# Revit family: OLYMPIA 24 X 96
name_source: partatom
category: Generic Models
units: mm (PartAtom-declared; Revit-internal decimal feet)

## family parameters
Can host rebar = No
Cut with Voids When Loaded = No
Host = Face
Maintain Annotation Orientation = No
Part Type = Normal
Room Calculation Point = No
Round Connector Dimension = Use Diameter
Shared = No

## types (11) — shared parameters
1/2 STICK = 4' - 0"
Default Elevation = 4' - 0"
PANEL LENGTH = 8' - 0"
PANEL MATERIAL = WF - PLYWOOD
PANEL WIDTH = 2' - 0"
STICKS PER WIDTH = 8

## per-type parameters (varying)
| type | CLADDING MATERIAL |
| OLYMPIA 24 X 96 - BONE | WF - CASCADES / OLYMPIA - BONE |
| OLYMPIA 24 X 96 - CITRINE | WF - CASCADES / OLYMPIA - CITRINE |
| OLYMPIA 24 X 96 - AUBURN | WF - CASCADES / OLYMPIA - AUBURN |
| OLYMPIA 24 X 96 - CLEAR | WF - CASCADES / OLYMPIA - CLEAR |
| OLYMPIA 24 X 96 - DOVE | WF - CASCADES / OLYMPIA - DOVE |
| OLYMPIA 24 X 96 - EARTHEN | WF - CASCADES / OLYMPIA - EARTHEN |
| OLYMPIA 24 X 96 - ESPRESSO | WF - CASCADES / OLYMPIA - ESPRESSO |
| OLYMPIA 24 X 96 - MONARCH | WF - CASCADES / OLYMPIA - MONARCH |
| OLYMPIA 24 X 96 -  RAVEN | WF - CASCADES / OLYMPIA - RAVEN |
| OLYMPIA 24 X 96 - SAGE | WF - CASCADES / OLYMPIA - SAGE |
| OLYMPIA 24 X 96 - SLATE | WF - CASCADES / OLYMPIA - SLATE |

## geometry (parser evidence)
native form markers: Sweep x5
no freeform markers — native parametric forms only
